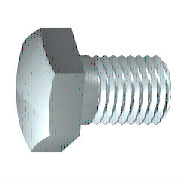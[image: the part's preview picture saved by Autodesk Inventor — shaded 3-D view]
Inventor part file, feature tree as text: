
AUTODESK INVENTOR PART (.ipt)
format: ipt  version: 2023.1 (Build 271208000, 208)  size: 191,488 bytes
history: native  units: mm (DEFAULTED — no unit token found)
features: sketch x3, extrude x1, chamfer x1, plane x1
ambient origin geometry x7: Origin, YZ Plane, XZ Plane, X Axis, Y Axis, Z Axis, Center Point
bodies: Solid1 (feature_tree), Body (feature_tree)
feature tree (6):
  extrude  "Head"  Depth=94.0mm
  chamfer  "Chamfer1"  Distance=9.2mm
  plane  "Work Plane1"
  sketch  "Sketch1"  dims[d0=100.0mm d1=94.0mm]
  sketch  "Sketch2"  dims[d2=16.0mm]
  sketch  "Sketch4"  dims[d12=90.0deg d3=9.2mm d4=0.0mm d5=30.0deg d21=90.0deg d6=1.2269mm d7=1.227mm d8=0.0mm d9=0.8001mm d10=22.49mm d11=24.0mm d13=1.227mm d14=16.0mm d15=94.0mm d16=0.0mm d19=24.0mm d55=45.0deg d57=0.0mm d58=0.0mm]
